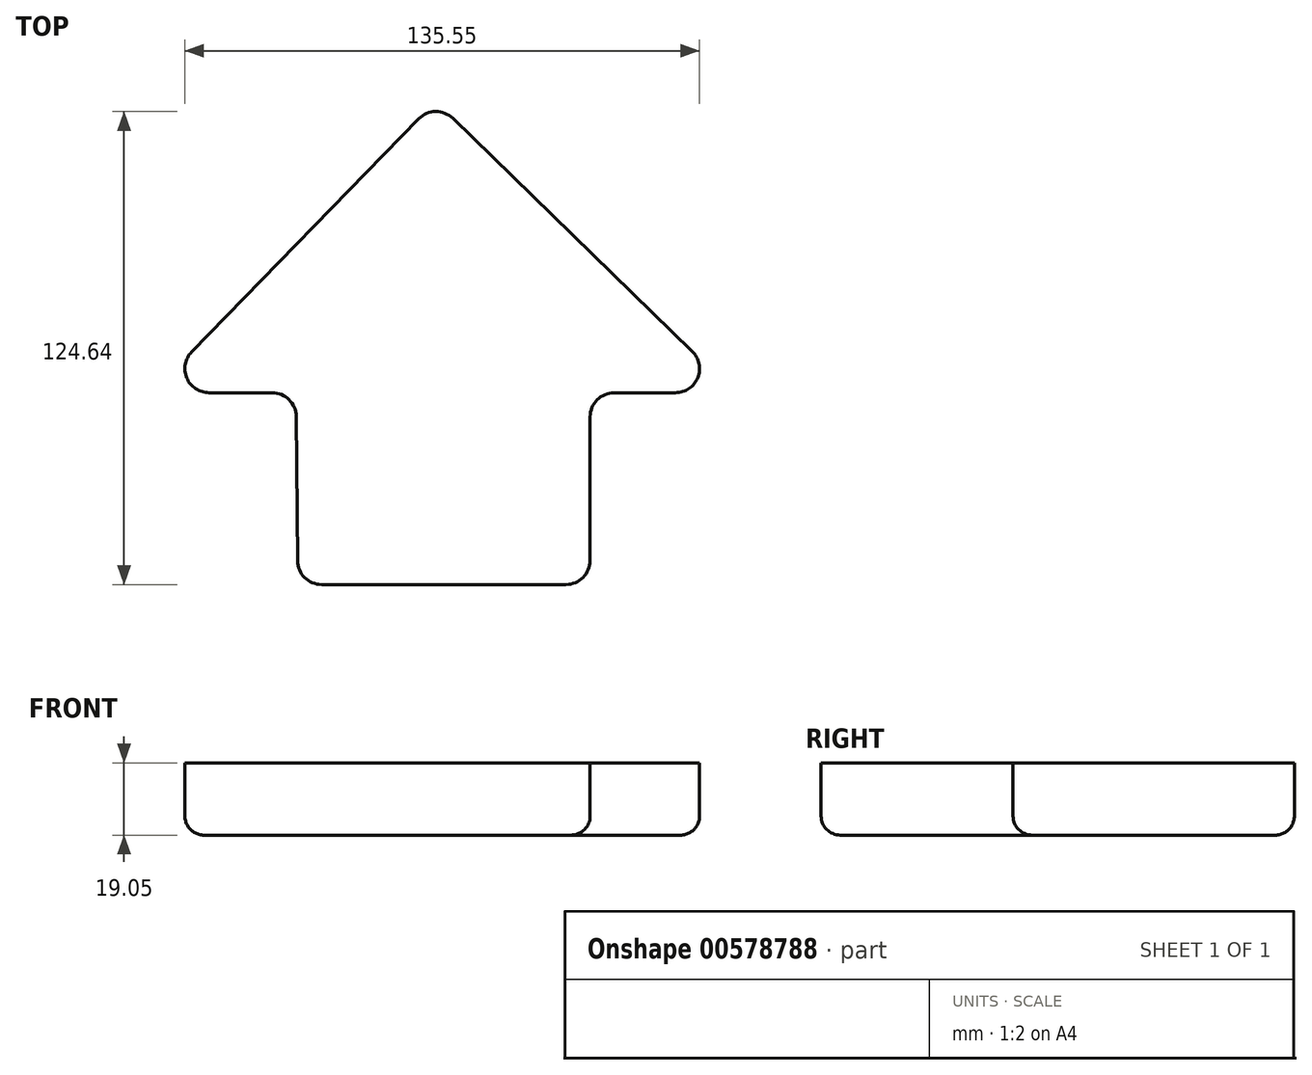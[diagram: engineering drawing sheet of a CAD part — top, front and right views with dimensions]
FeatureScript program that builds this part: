
annotation { "Feature Type Name" : "Feature", "Feature Type Description" : "" }
export const myFeature = defineFeature(function(context is Context, id is Id, definition is map)
    precondition{}
    {
        {
            var Q0;
            Q0=qCreatedBy(makeId("Top.planeOp"),FACE);
            var sketch = newSketch(context, id + "F0", { "sketchPlane" : qUnion([Q0])});
            skLineSegment(sketch, "E0", {"start": v(45.33, 2.9) * mm, "end": v(61.46, 2.9) * mm});
            skLineSegment(sketch, "E1", {"start": v(65.89, 13.8) * mm, "end": v(2.82, 75.2) * mm});
            skLineSegment(sketch, "E2", {"start": v(-6.16, 75.09) * mm, "end": v(-65.94, 13.69) * mm});
            skLineSegment(sketch, "E3", {"start": v(-61.39, 2.9) * mm, "end": v(-44.76, 2.9) * mm});
            skLineSegment(sketch, "E4", {"start": v(32.63, -47.63) * mm, "end": v(-31.74, -47.63) * mm});
            skLineSegment(sketch, "E5", {"start": v(-38.1, -41.34) * mm, "end": v(-38.4, -3.39) * mm});
            skLineSegment(sketch, "E6", {"start": v(38.98, -3.44) * mm, "end": v(38.98, -41.28) * mm});
            skPoint(sketch, "E7.visualSharp", {"position": v(77.08, 2.9) * mm});
            skArc(sketch, "E7.filletArc", {"start": v(61.46, 2.9) * mm, "mid": v(67.34, 6.87) * mm, "end": v(65.89, 13.8) * mm});
            skPoint(sketch, "E8.visualSharp", {"position": v(-76.43, 2.9) * mm});
            skArc(sketch, "E8.filletArc", {"start": v(-65.94, 13.69) * mm, "mid": v(-67.24, 6.8) * mm, "end": v(-61.39, 2.9) * mm});
            skPoint(sketch, "E9.visualSharp", {"position": v(-1.73, 79.64) * mm});
            skArc(sketch, "E9.filletArc", {"start": v(2.82, 75.2) * mm, "mid": v(-1.7, 77) * mm, "end": v(-6.16, 75.09) * mm});
            skPoint(sketch, "E10.visualSharp", {"position": v(-38.04, -47.63) * mm});
            skArc(sketch, "E10.filletArc", {"start": v(-38.1, -41.34) * mm, "mid": v(-36.21, -45.8) * mm, "end": v(-31.74, -47.63) * mm});
            skPoint(sketch, "E11.visualSharp", {"position": v(38.98, -47.63) * mm});
            skArc(sketch, "E11.filletArc", {"start": v(32.63, -47.63) * mm, "mid": v(37.12, -45.77) * mm, "end": v(38.98, -41.28) * mm});
            skPoint(sketch, "E12.visualSharp", {"position": v(-38.46, 2.9) * mm});
            skArc(sketch, "E12.filletArc", {"start": v(-38.4, -3.39) * mm, "mid": v(-40.29, 1.07) * mm, "end": v(-44.76, 2.9) * mm});
            skPoint(sketch, "E13.visualSharp", {"position": v(38.98, 2.9) * mm});
            skArc(sketch, "E13.filletArc", {"start": v(45.33, 2.9) * mm, "mid": v(40.84, 1.05) * mm, "end": v(38.98, -3.44) * mm});
            skSolve(sketch);
        }
        {
            var Q0;
            Q0=makeQuery(id+"F0.imprint","IMPRINT",FACE,{"disambiguationData":[TD([[makeQuery(id+"F0.imprint","IMPRINT",EDGE,{"derivedFrom":sQuery(id+"F0.wireOp",EDGE,"E0")}),1.0]])]});
            extrude(context, id + "F1", {"entities" : qUnion([Q0]), "depth" : 19.05 * mm, "offsetDistance" : 25.4 * mm});
        }
        {
            var Q0;
            Q0=makeQuery(id+"F1.opExtrude","CAP_FACE",FACE,{"disambiguationData":[OSD([sQuery(id+"F0.wireOp",EDGE,"E0"),sQuery(id+"F0.wireOp",EDGE,"E1"),sQuery(id+"F0.wireOp",EDGE,"E2"),sQuery(id+"F0.wireOp",EDGE,"E3"),sQuery(id+"F0.wireOp",EDGE,"E4"),sQuery(id+"F0.wireOp",EDGE,"E5"),sQuery(id+"F0.wireOp",EDGE,"E6"),sQuery(id+"F0.wireOp",EDGE,"E7.filletArc"),sQuery(id+"F0.wireOp",EDGE,"E8.filletArc"),sQuery(id+"F0.wireOp",EDGE,"E9.filletArc"),sQuery(id+"F0.wireOp",EDGE,"E10.filletArc"),sQuery(id+"F0.wireOp",EDGE,"E11.filletArc"),sQuery(id+"F0.wireOp",EDGE,"E12.filletArc"),sQuery(id+"F0.wireOp",EDGE,"E13.filletArc")])],"isStart":true});
            fillet(context, id + "F2", {"entities" : qUnion([Q0]), "radius" : 5.08 * mm, "tangentPropagation" : true, "allowEdgeOverflow" : false});
        }
    });
